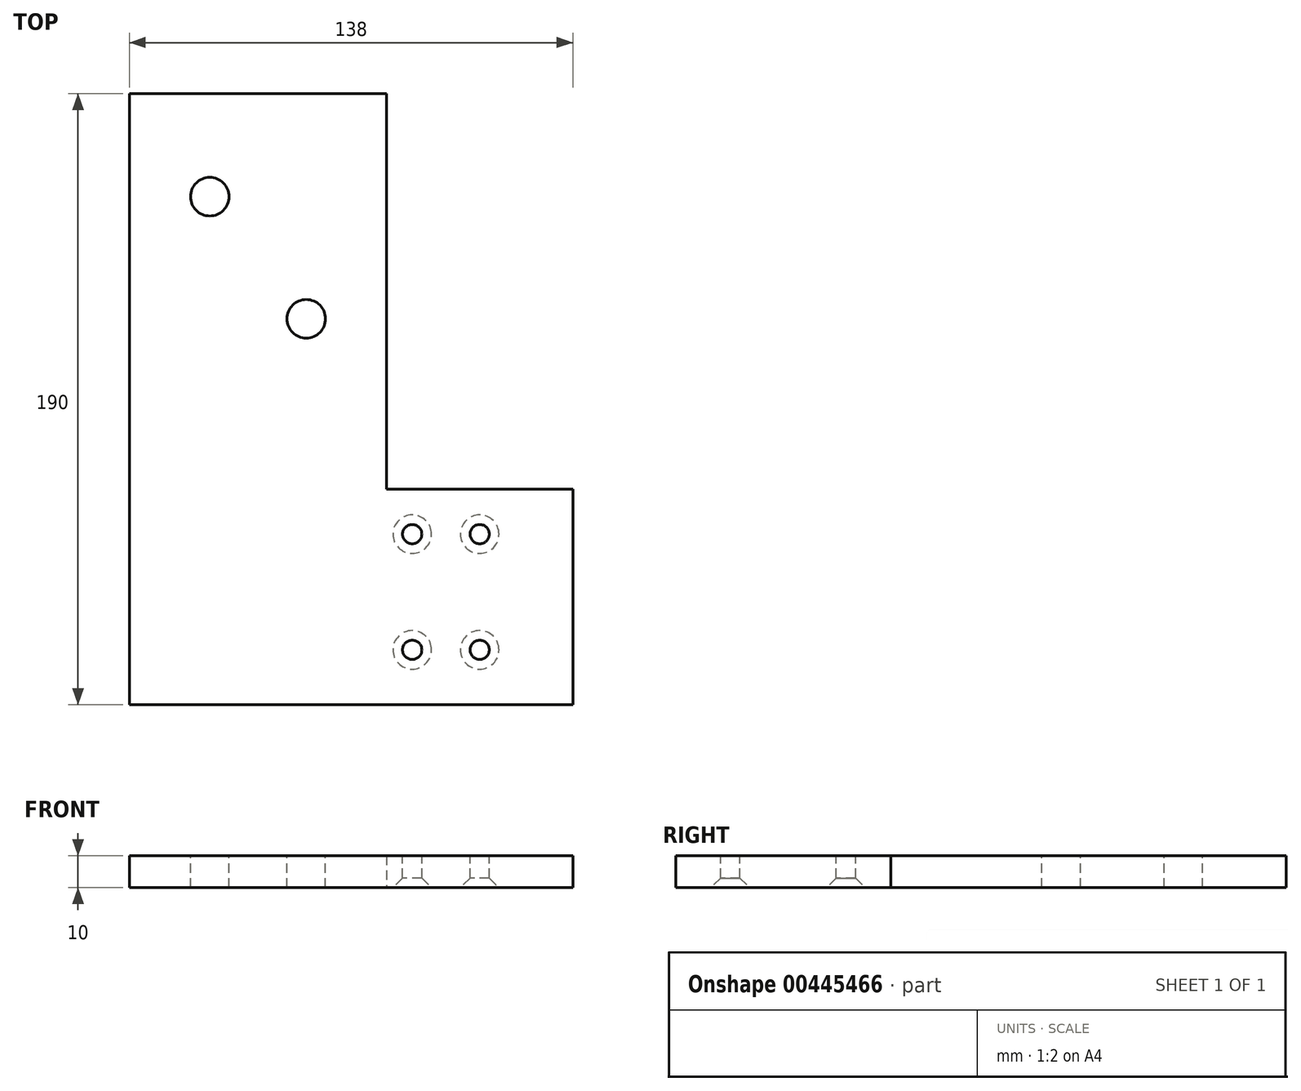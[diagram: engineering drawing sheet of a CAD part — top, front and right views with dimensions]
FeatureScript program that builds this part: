
annotation { "Feature Type Name" : "Feature", "Feature Type Description" : "" }
export const myFeature = defineFeature(function(context is Context, id is Id, definition is map)
    precondition{}
    {
        {
            var Q0;
            Q0=qCreatedBy(makeId("Top.planeOp"),FACE);
            var sketch = newSketch(context, id + "F0", { "sketchPlane" : qUnion([Q0])});
            skLineSegment(sketch, "E0.bottom", {"start": v(40, -95) * mm, "end": v(-40, -95) * mm});
            skLineSegment(sketch, "E0.top", {"start": v(40, 95) * mm, "end": v(-40, 95) * mm});
            skLineSegment(sketch, "E0.left", {"start": v(40, -95) * mm, "end": v(40, 95) * mm});
            skLineSegment(sketch, "E0.right", {"start": v(-40, -95) * mm, "end": v(-40, 95) * mm});
            skPoint(sketch, "E0.middle", {"position": v(0, 0) * mm});
            skLineSegment(sketch, "E1.bottom", {"start": v(40, -95) * mm, "end": v(98, -95) * mm});
            skLineSegment(sketch, "E1.top", {"start": v(40, -28) * mm, "end": v(98, -28) * mm});
            skLineSegment(sketch, "E1.left", {"start": v(40, -95) * mm, "end": v(40, -28) * mm});
            skLineSegment(sketch, "E1.right", {"start": v(98, -95) * mm, "end": v(98, -28) * mm});
            skSolve(sketch);
        }
        {
            var Q0;
            Q0=qSketchRegion(id+"F0",true);
            extrude(context, id + "F1", {"entities" : qUnion([Q0]), "depth" : 10 * mm, "offsetDistance" : 25 * mm});
        }
        {
            var Q0;
            Q0=makeQuery(id+"F1.opExtrude","CAP_FACE",FACE,{"disambiguationData":[OSD([sQuery(id+"F0.wireOp",EDGE,"E0.bottom"),sQuery(id+"F0.wireOp",EDGE,"E0.top"),sQuery(id+"F0.wireOp",EDGE,"E0.left"),sQuery(id+"F0.wireOp",EDGE,"E0.right")])],"isStart":false});
            var sketch = newSketch(context, id + "F2", { "sketchPlane" : qUnion([Q0])});
            skCircle(sketch, "E2", {"center": v(48, -78) * mm, "radius": 3 * mm});
            skCircle(sketch, "E3.0.1.0", {"center": v(48, -42) * mm, "radius": 3 * mm});
            skCircle(sketch, "E3.1.0.0", {"center": v(69, -78) * mm, "radius": 3 * mm});
            skCircle(sketch, "E3.1.1.0", {"center": v(69, -42) * mm, "radius": 3 * mm});
            skLineSegment(sketch, "E3.direction1", {"start": v(48, -78) * mm, "end": v(69, -78) * mm, "construction": true});
            skLineSegment(sketch, "E3.direction2", {"start": v(48, -78) * mm, "end": v(48, -42) * mm, "construction": true});
            skCircle(sketch, "E4", {"center": v(-15, 63) * mm, "radius": 6 * mm});
            skCircle(sketch, "E5", {"center": v(15, 25) * mm, "radius": 6 * mm});
            skSolve(sketch);
        }
        {
            var Q0;
            Q0=qSketchRegion(id+"F2",true);
            extrude(context, id + "F3", {"entities" : qUnion([Q0]), "operationType" : NewBodyOperationType.REMOVE, "oppositeDirection" : true, "depth" : 25 * mm, "offsetDistance" : 25 * mm});
        }
        {
            var Q0;
            Q0=makeQuery(id+"F3.boolean.opBoolean","INTERSECT",EDGE,{"derivedFrom":[makeQuery(id+"F1.opExtrude","CAP_FACE",FACE,{"disambiguationData":[OSD([sQuery(id+"F0.wireOp",EDGE,"E0.bottom"),sQuery(id+"F0.wireOp",EDGE,"E0.top"),sQuery(id+"F0.wireOp",EDGE,"E0.left"),sQuery(id+"F0.wireOp",EDGE,"E0.right"),sQuery(id+"F0.wireOp",EDGE,"E1.bottom"),sQuery(id+"F0.wireOp",EDGE,"E1.top"),sQuery(id+"F0.wireOp",EDGE,"E1.right")])],"isStart":true}),makeQuery(id+"F3.opExtrude","SWEPT_FACE",FACE,{"disambiguationData":[OSD([sQuery(id+"F2.wireOp",EDGE,"E3.1.0.0")])]})]});
            var Q1;
            Q1=makeQuery(id+"F3.boolean.opBoolean","INTERSECT",EDGE,{"derivedFrom":[makeQuery(id+"F1.opExtrude","CAP_FACE",FACE,{"disambiguationData":[OSD([sQuery(id+"F0.wireOp",EDGE,"E0.bottom"),sQuery(id+"F0.wireOp",EDGE,"E0.top"),sQuery(id+"F0.wireOp",EDGE,"E0.left"),sQuery(id+"F0.wireOp",EDGE,"E0.right"),sQuery(id+"F0.wireOp",EDGE,"E1.bottom"),sQuery(id+"F0.wireOp",EDGE,"E1.top"),sQuery(id+"F0.wireOp",EDGE,"E1.right")])],"isStart":true}),makeQuery(id+"F3.opExtrude","SWEPT_FACE",FACE,{"disambiguationData":[OSD([sQuery(id+"F2.wireOp",EDGE,"E2")])]})]});
            var Q2;
            Q2=makeQuery(id+"F3.boolean.opBoolean","INTERSECT",EDGE,{"derivedFrom":[makeQuery(id+"F1.opExtrude","CAP_FACE",FACE,{"disambiguationData":[OSD([sQuery(id+"F0.wireOp",EDGE,"E0.bottom"),sQuery(id+"F0.wireOp",EDGE,"E0.top"),sQuery(id+"F0.wireOp",EDGE,"E0.left"),sQuery(id+"F0.wireOp",EDGE,"E0.right"),sQuery(id+"F0.wireOp",EDGE,"E1.bottom"),sQuery(id+"F0.wireOp",EDGE,"E1.top"),sQuery(id+"F0.wireOp",EDGE,"E1.right")])],"isStart":true}),makeQuery(id+"F3.opExtrude","SWEPT_FACE",FACE,{"disambiguationData":[OSD([sQuery(id+"F2.wireOp",EDGE,"E3.0.1.0")])]})]});
            var Q3;
            Q3=makeQuery(id+"F3.boolean.opBoolean","INTERSECT",EDGE,{"derivedFrom":[makeQuery(id+"F1.opExtrude","CAP_FACE",FACE,{"disambiguationData":[OSD([sQuery(id+"F0.wireOp",EDGE,"E0.bottom"),sQuery(id+"F0.wireOp",EDGE,"E0.top"),sQuery(id+"F0.wireOp",EDGE,"E0.left"),sQuery(id+"F0.wireOp",EDGE,"E0.right"),sQuery(id+"F0.wireOp",EDGE,"E1.bottom"),sQuery(id+"F0.wireOp",EDGE,"E1.top"),sQuery(id+"F0.wireOp",EDGE,"E1.right")])],"isStart":true}),makeQuery(id+"F3.opExtrude","SWEPT_FACE",FACE,{"disambiguationData":[OSD([sQuery(id+"F2.wireOp",EDGE,"E3.1.1.0")])]})]});
            chamfer(context, id + "F4", {"entities" : qUnion([Q0, Q1, Q2, Q3]), "width" : 3 * mm, "tangentPropagation" : true});
        }
    });
